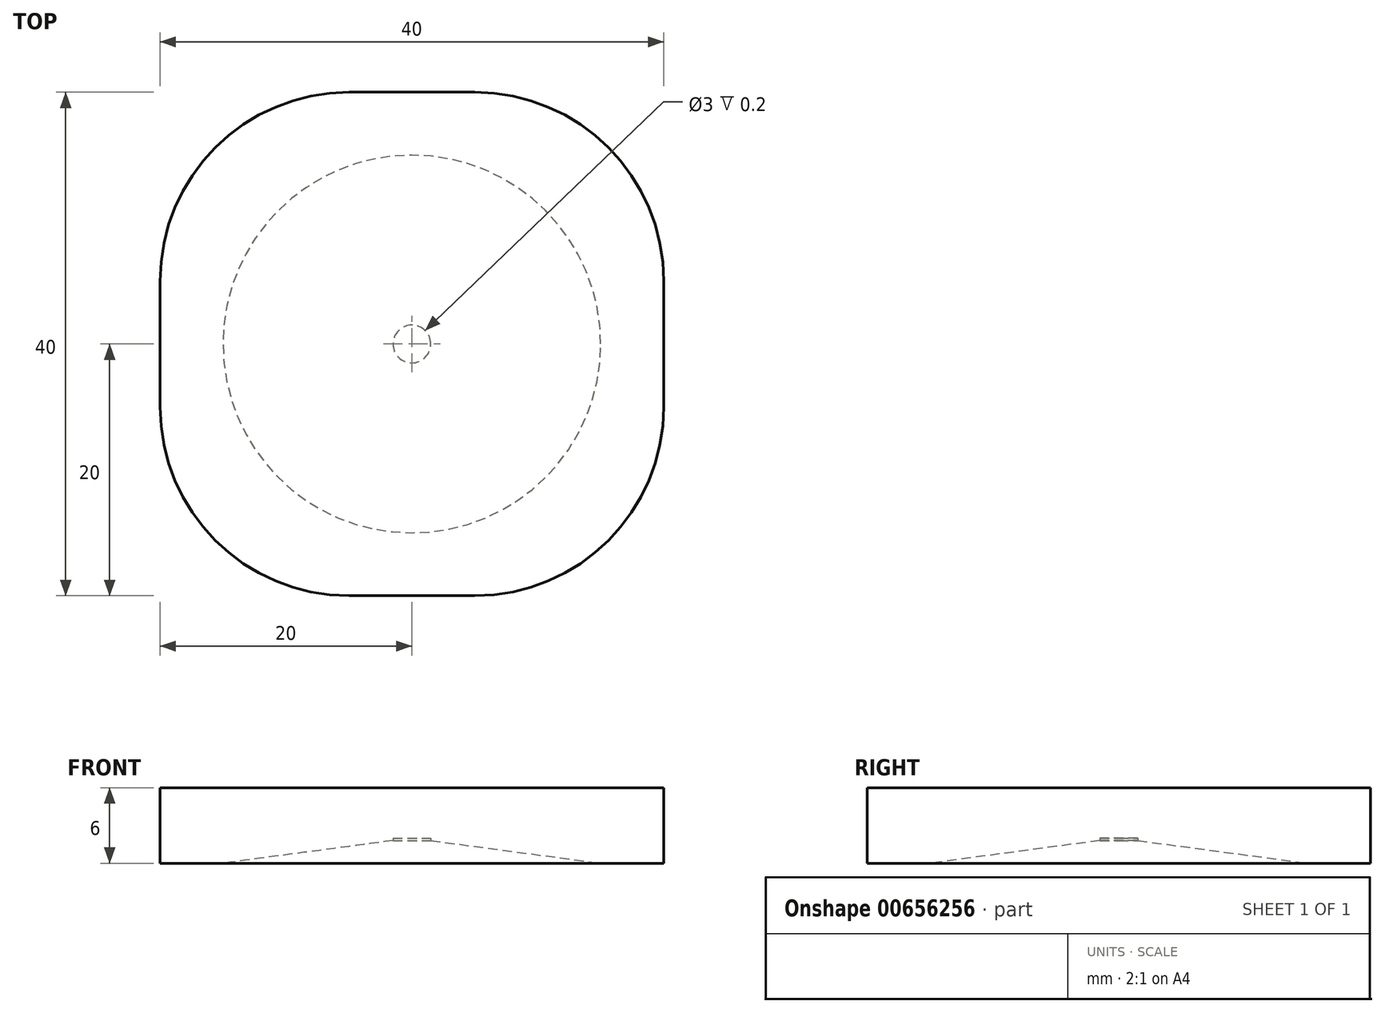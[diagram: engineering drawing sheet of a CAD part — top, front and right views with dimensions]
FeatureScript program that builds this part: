
annotation { "Feature Type Name" : "Feature", "Feature Type Description" : "" }
export const myFeature = defineFeature(function(context is Context, id is Id, definition is map)
    precondition{}
    {
        {
            var Q0;
            Q0=qCreatedBy(makeId("Top.planeOp"),FACE);
            var sketch = newSketch(context, id + "F0", { "sketchPlane" : qUnion([Q0])});
            skLineSegment(sketch, "E0.bottom", {"start": v(20, 20) * mm, "end": v(-20, 20) * mm});
            skLineSegment(sketch, "E0.top", {"start": v(20, -20) * mm, "end": v(-20, -20) * mm});
            skLineSegment(sketch, "E0.left", {"start": v(20, 20) * mm, "end": v(20, -20) * mm});
            skLineSegment(sketch, "E0.right", {"start": v(-20, 20) * mm, "end": v(-20, -20) * mm});
            skPoint(sketch, "E0.middle", {"position": v(0, 0) * mm});
            skSolve(sketch);
        }
        {
            var Q0;
            Q0=makeQuery(id+"F0.imprint","IMPRINT",FACE,{"disambiguationData":[TD([[makeQuery(id+"F0.imprint","IMPRINT",EDGE,{"derivedFrom":sQuery(id+"F0.wireOp",EDGE,"E0.bottom")}),1.0]])]});
            extrude(context, id + "F1", {"entities" : qUnion([Q0]), "depth" : 6 * mm, "offsetDistance" : 25 * mm});
        }
        {
            var Q0;
            Q0=makeQuery(id+"F1.opExtrude","SWEPT_EDGE",EDGE,{"disambiguationData":[OSD([sQuery(id+"F0.wireOp",EDGE,"E0.bottom"),sQuery(id+"F0.wireOp",EDGE,"E0.right")])]});
            var Q1;
            Q1=makeQuery(id+"F1.opExtrude","SWEPT_EDGE",EDGE,{"disambiguationData":[OSD([sQuery(id+"F0.wireOp",EDGE,"E0.bottom"),sQuery(id+"F0.wireOp",EDGE,"E0.left")])]});
            var Q2;
            Q2=makeQuery(id+"F1.opExtrude","SWEPT_EDGE",EDGE,{"disambiguationData":[OSD([sQuery(id+"F0.wireOp",EDGE,"E0.top"),sQuery(id+"F0.wireOp",EDGE,"E0.left")])]});
            var Q3;
            Q3=makeQuery(id+"F1.opExtrude","SWEPT_EDGE",EDGE,{"disambiguationData":[OSD([sQuery(id+"F0.wireOp",EDGE,"E0.top"),sQuery(id+"F0.wireOp",EDGE,"E0.right")])]});
            fillet(context, id + "F2", {"entities" : qUnion([Q0, Q1, Q2, Q3]), "radius" : 15 * mm, "tangentPropagation" : true, "allowEdgeOverflow" : false});
        }
        {
            var Q0;
            Q0=makeQuery(id+"F1.opExtrude","CAP_FACE",FACE,{"disambiguationData":[OSD([sQuery(id+"F0.wireOp",EDGE,"E0.bottom"),sQuery(id+"F0.wireOp",EDGE,"E0.top"),sQuery(id+"F0.wireOp",EDGE,"E0.left"),sQuery(id+"F0.wireOp",EDGE,"E0.right")])],"isStart":true});
            var sketch = newSketch(context, id + "F3", { "sketchPlane" : qUnion([Q0])});
            skCircle(sketch, "E1", {"center": v(0, 0) * mm, "radius": 1.5 * mm});
            skSolve(sketch);
        }
        {
            var Q0;
            Q0=makeQuery(id+"F3.imprint","IMPRINT",FACE,{"disambiguationData":[TD([[makeQuery(id+"F3.imprint","IMPRINT",EDGE,{"derivedFrom":sQuery(id+"F3.wireOp",EDGE,"E1")}),1.0]])]});
            extrude(context, id + "F4", {"entities" : qUnion([Q0]), "operationType" : NewBodyOperationType.REMOVE, "oppositeDirection" : true, "depth" : 2 * mm, "offsetDistance" : 25 * mm});
        }
        {
            var Q0;
            Q0=qCreatedBy(makeId("Front.planeOp"),FACE);
            var sketch = newSketch(context, id + "F5", { "sketchPlane" : qUnion([Q0])});
            skLineSegment(sketch, "E2", {"start": v(0, 2) * mm, "end": v(0, 0) * mm});
            skLineSegment(sketch, "E3", {"start": v(0, 0) * mm, "end": v(-15, 0) * mm});
            skLineSegment(sketch, "E4", {"start": v(-15, 0) * mm, "end": v(0, 2) * mm});
            skSolve(sketch);
        }
        {
            var Q0;
            Q0=makeQuery(id+"F5.imprint","IMPRINT",FACE,{"disambiguationData":[TD([[makeQuery(id+"F5.imprint","IMPRINT",EDGE,{"derivedFrom":sQuery(id+"F5.wireOp",EDGE,"E2")}),-1.0]])]});
            var Q1;
            Q1=sQuery(id+"F5.wireOp",EDGE,"E2");
            revolve(context, id + "F6", {"operationType" : NewBodyOperationType.REMOVE, "entities" : qUnion([Q0]), "axis" : qUnion([Q1]), "revolveType" : RevolveType.FULL, "oppositeDirection" : true});
        }
    });
